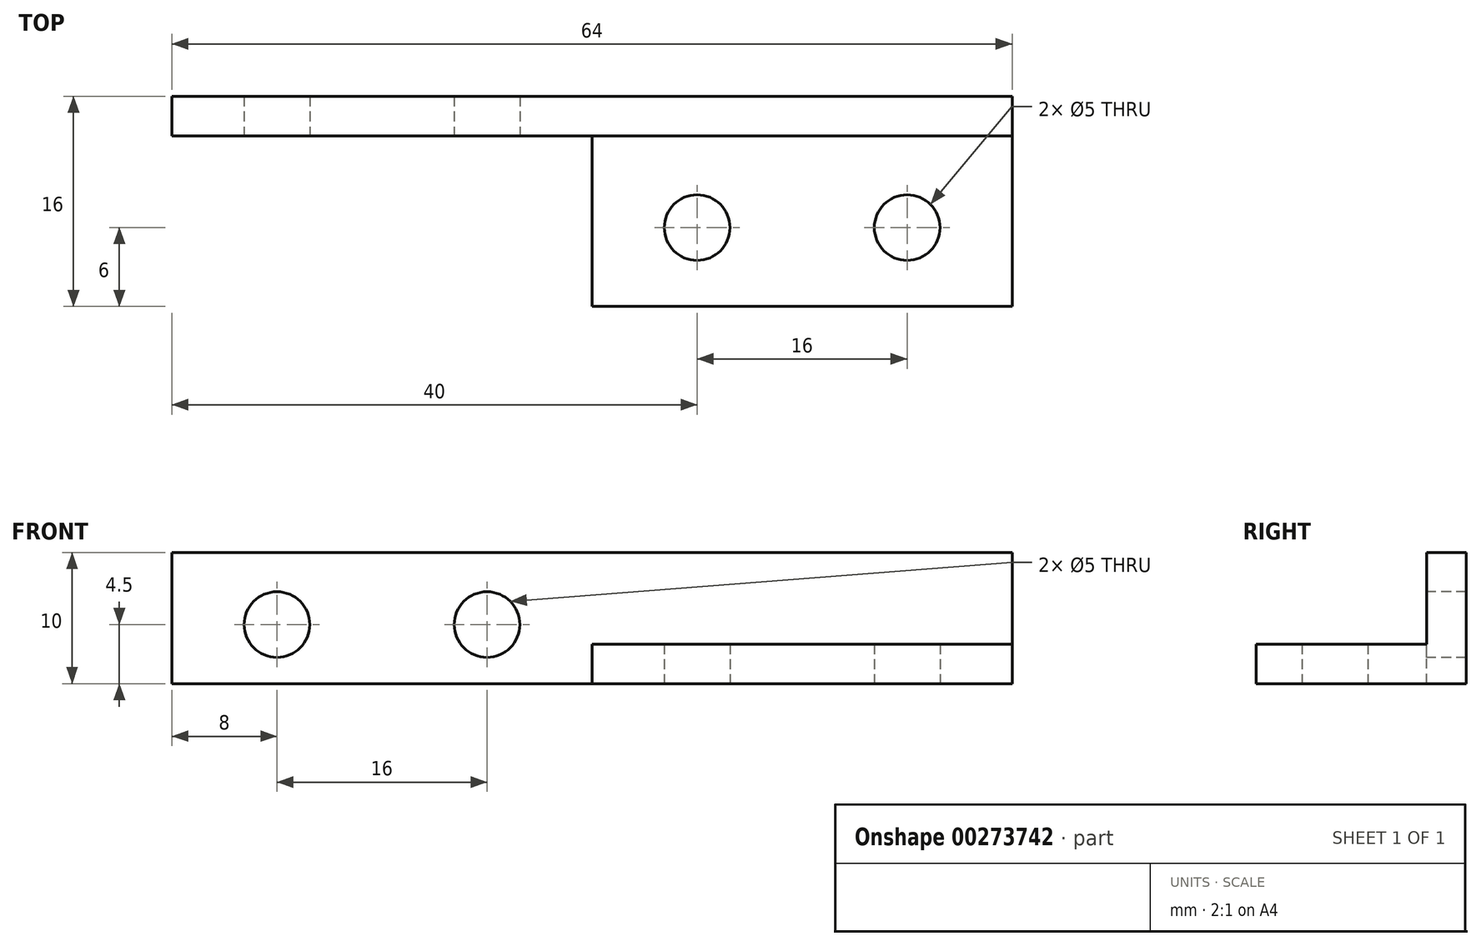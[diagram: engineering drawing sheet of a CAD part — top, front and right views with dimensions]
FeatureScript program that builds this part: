
annotation { "Feature Type Name" : "Feature", "Feature Type Description" : "" }
export const myFeature = defineFeature(function(context is Context, id is Id, definition is map)
    precondition{}
    {
        {
            var Q0;
            Q0=qCreatedBy(makeId("Top.planeOp"),FACE);
            var sketch = newSketch(context, id + "F0", { "sketchPlane" : qUnion([Q0])});
            skLineSegment(sketch, "E0.bottom", {"start": v(-16, 8) * mm, "end": v(16, 8) * mm});
            skLineSegment(sketch, "E0.top", {"start": v(-16, -8) * mm, "end": v(16, -8) * mm});
            skLineSegment(sketch, "E0.left", {"start": v(-16, 8) * mm, "end": v(-16, -8) * mm});
            skLineSegment(sketch, "E0.right", {"start": v(16, 8) * mm, "end": v(16, -8) * mm});
            skPoint(sketch, "E0.middle", {"position": v(0, 0) * mm});
            skCircle(sketch, "E1", {"center": v(8, -2) * mm, "radius": 2.5 * mm});
            skCircle(sketch, "E2", {"center": v(-8, -2) * mm, "radius": 2.5 * mm});
            skSolve(sketch);
        }
        {
            var Q0;
            Q0=makeQuery(id+"F0.imprint","IMPRINT",FACE,{"disambiguationData":[TD([[makeQuery(id+"F0.imprint","IMPRINT",EDGE,{"derivedFrom":sQuery(id+"F0.wireOp",EDGE,"E0.bottom")}),-1.0]])]});
            extrude(context, id + "F1", {"entities" : qUnion([Q0]), "depth" : 3 * mm});
        }
        {
            var Q0;
            Q0=makeQuery(id+"F1.opExtrude","CAP_FACE",FACE,{"disambiguationData":[OSD([sQuery(id+"F0.wireOp",EDGE,"E0.bottom"),sQuery(id+"F0.wireOp",EDGE,"E0.top"),sQuery(id+"F0.wireOp",EDGE,"E0.left"),sQuery(id+"F0.wireOp",EDGE,"E0.right"),sQuery(id+"F0.wireOp",EDGE,"E1"),sQuery(id+"F0.wireOp",EDGE,"E2")])],"isStart":false});
            var sketch = newSketch(context, id + "F2", { "sketchPlane" : qUnion([Q0])});
            skLineSegment(sketch, "E3.bottom", {"start": v(16, 8) * mm, "end": v(-16, 8) * mm});
            skLineSegment(sketch, "E3.top", {"start": v(16, 5) * mm, "end": v(-16, 5) * mm});
            skLineSegment(sketch, "E3.left", {"start": v(16, 8) * mm, "end": v(16, 5) * mm});
            skLineSegment(sketch, "E3.right", {"start": v(-16, 8) * mm, "end": v(-16, 5) * mm});
            skPoint(sketch, "E3.middle", {"position": v(0, 6.5) * mm});
            skSolve(sketch);
        }
        {
            var Q0;
            Q0=makeQuery(id+"F2.imprint","IMPRINT",FACE,{"disambiguationData":[TD([[makeQuery(id+"F2.imprint","IMPRINT",EDGE,{"derivedFrom":sQuery(id+"F2.wireOp",EDGE,"E3.bottom")}),-1.0]])]});
            extrude(context, id + "F3", {"entities" : qUnion([Q0]), "operationType" : NewBodyOperationType.ADD, "depth" : 7 * mm});
        }
        {
            var Q0;
            Q0=makeQuery(id+"F3.boolean.opBoolean","MERGE",FACE,{"derivedFrom":[makeQuery(id+"F1.opExtrude","SWEPT_FACE",FACE,{"disambiguationData":[OSD([sQuery(id+"F0.wireOp",EDGE,"E0.left")])]}),makeQuery(id+"F3.opExtrude","SWEPT_FACE",FACE,{"disambiguationData":[OSD([sQuery(id+"F2.wireOp",EDGE,"E3.right")])]})]});
            var sketch = newSketch(context, id + "F4", { "sketchPlane" : qUnion([Q0])});
            skLineSegment(sketch, "E4.bottom", {"start": v(-8, 0) * mm, "end": v(-5, 0) * mm});
            skLineSegment(sketch, "E4.top", {"start": v(-8, 10) * mm, "end": v(-5, 10) * mm});
            skLineSegment(sketch, "E4.left", {"start": v(-8, 0) * mm, "end": v(-8, 10) * mm});
            skLineSegment(sketch, "E4.right", {"start": v(-5, 0) * mm, "end": v(-5, 10) * mm});
            skSolve(sketch);
        }
        {
            var Q0;
            {var subQ3=sQuery(id+"F4.wireOp",EDGE,"E4.bottom");Q0=makeQuery(id+"F4.imprint","IMPRINT",FACE,{"disambiguationData":[TD([[makeQuery(id+"F4.imprint","IMPRINT",EDGE,{"derivedFrom":subQ3}),1.0]])]});}
            extrude(context, id + "F5", {"entities" : qUnion([Q0]), "operationType" : NewBodyOperationType.ADD, "depth" : 32 * mm});
        }
        {
            var Q0;
            Q0=makeQuery(id+"F5.boolean.opBoolean","MERGE",FACE,{"derivedFrom":[makeQuery(id+"F3.opExtrude","SWEPT_FACE",FACE,{"disambiguationData":[OSD([sQuery(id+"F2.wireOp",EDGE,"E3.top")])]}),makeQuery(id+"F5.opExtrude","SWEPT_FACE",FACE,{"disambiguationData":[OSD([sQuery(id+"F4.wireOp",EDGE,"E4.right")])]})]});
            var sketch = newSketch(context, id + "F6", { "sketchPlane" : qUnion([Q0])});
            skCircle(sketch, "E5", {"center": v(-40, 4.5) * mm, "radius": 2.5 * mm});
            skCircle(sketch, "E6", {"center": v(-24, 4.5) * mm, "radius": 2.5 * mm});
            skSolve(sketch);
        }
        {
            var Q0;
            Q0 = qSketchRegion(id + "F6", true);
            extrude(context, id + "F7", {"entities" : qUnion([Q0]), "operationType" : NewBodyOperationType.REMOVE, "oppositeDirection" : true, "depth" : 3 * mm});
        }
    });
